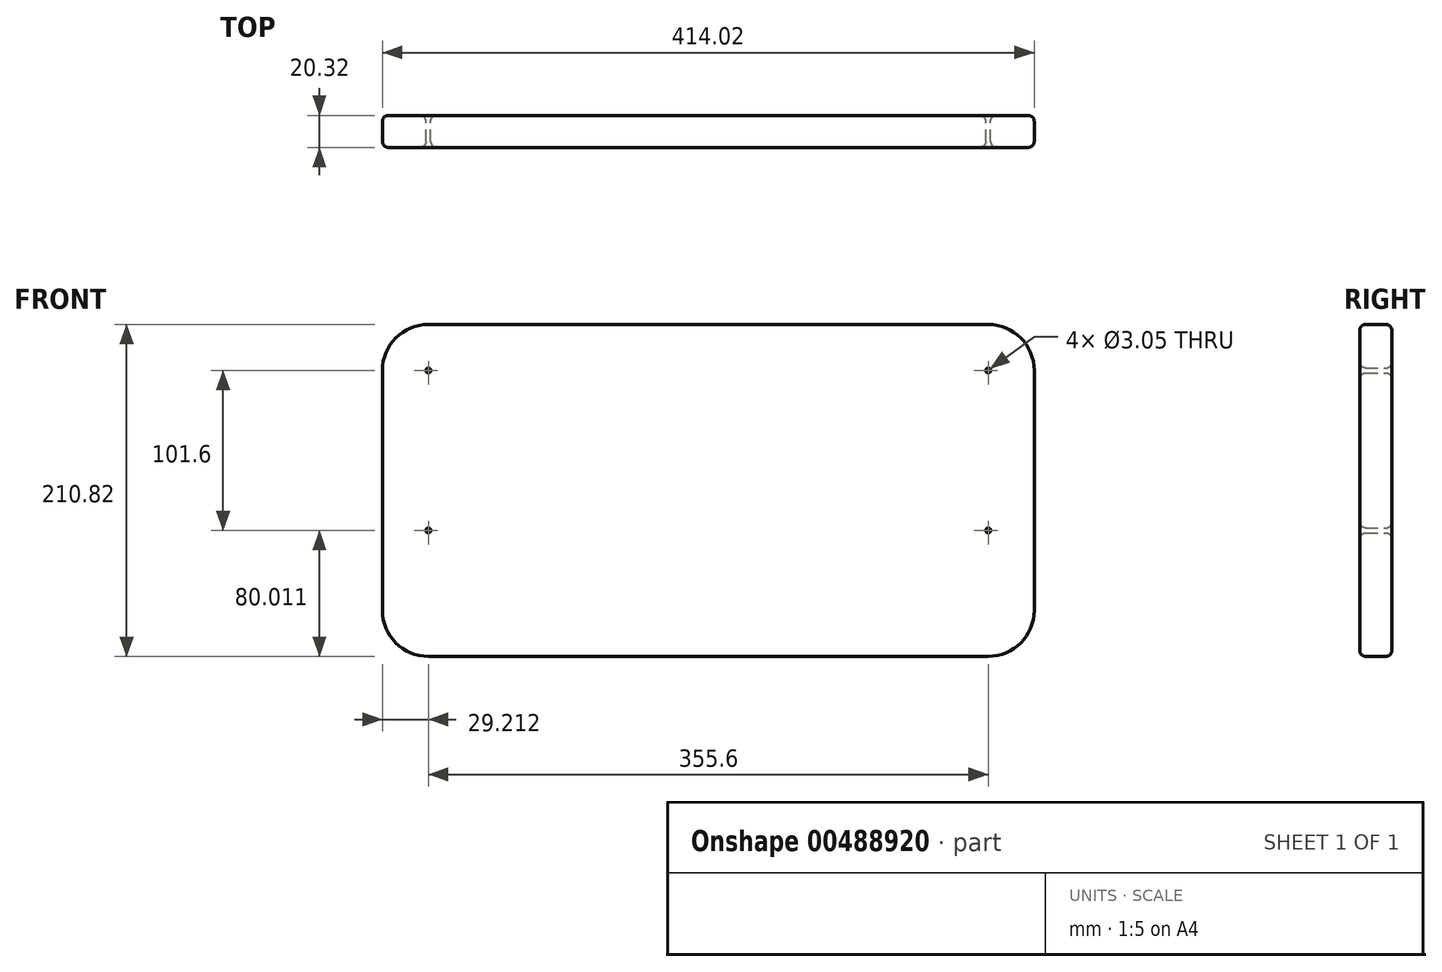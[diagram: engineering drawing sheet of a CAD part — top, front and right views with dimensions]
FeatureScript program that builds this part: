
annotation { "Feature Type Name" : "Feature", "Feature Type Description" : "" }
export const myFeature = defineFeature(function(context is Context, id is Id, definition is map)
    precondition{}
    {
        {
            var Q0;
            Q0=qCreatedBy(makeId("Front.planeOp"),FACE);
            var sketch = newSketch(context, id + "F0", { "sketchPlane" : qUnion([Q0])});
            skArc(sketch, "E0", {"start": v(-339, -245.28) * mm, "mid": v(-359.66, -253.83) * mm, "end": v(-368.22, -274.49) * mm});
            skArc(sketch, "E1", {"start": v(16.6, -245.28) * mm, "mid": v(37.25, -253.83) * mm, "end": v(45.8, -274.49) * mm});
            skLineSegment(sketch, "E2", {"start": v(-339, -245.28) * mm, "end": v(16.6, -245.28) * mm});
            skArc(sketch, "E3", {"start": v(-368.22, -426.89) * mm, "mid": v(-359.66, -447.54) * mm, "end": v(-339, -456.1) * mm});
            skArc(sketch, "E4", {"start": v(16.6, -456.1) * mm, "mid": v(37.25, -447.54) * mm, "end": v(45.8, -426.89) * mm});
            skLineSegment(sketch, "E5", {"start": v(-368.22, -274.49) * mm, "end": v(-368.22, -426.89) * mm});
            skLineSegment(sketch, "E6", {"start": v(-339, -456.1) * mm, "end": v(16.6, -456.1) * mm});
            skLineSegment(sketch, "E7", {"start": v(45.8, -274.49) * mm, "end": v(45.8, -426.89) * mm});
            skCircle(sketch, "E8", {"center": v(-339, -274.49) * mm, "radius": 1.52 * mm});
            skCircle(sketch, "E9", {"center": v(16.6, -274.49) * mm, "radius": 1.52 * mm});
            skCircle(sketch, "E10", {"center": v(-339, -376.09) * mm, "radius": 1.52 * mm});
            skPoint(sketch, "E11", {"position": v(-161.2, -245.28) * mm});
            skCircle(sketch, "E12.MirrorC", {"center": v(16.6, -376.09) * mm, "radius": 1.52 * mm});
            skSolve(sketch);
        }
        {
            var Q0;
            {var subQ1=sQuery(id+"F0.wireOp",EDGE,"sNFvKARg-ezan-HJEH-VfS0-Z6MDpd9502FD.top");Q0=makeQuery(id+"F0.imprint","IMPRINT",FACE,{"disambiguationData":[TD([[makeQuery(id+"F0.imprint","IMPRINT",EDGE,{"derivedFrom":subQ1}),1.0]])]});}
            var Q1;
            Q1=makeQuery(id+"F0.imprint","IMPRINT",FACE,{"disambiguationData":[TD([[makeQuery(id+"F0.imprint","IMPRINT",EDGE,{"derivedFrom":sQuery(id+"F0.wireOp",EDGE,"E0")}),1.0]])]});
            var Q2;
            {var subQ1=sQuery(id+"F0.wireOp",EDGE,"sNFvKARg-ezan-HJEH-VfS0-Z6MDpd9502FD.top");Q2=makeQuery(id+"F0.imprint","IMPRINT",FACE,{"disambiguationData":[TD([[makeQuery(id+"F0.imprint","IMPRINT",EDGE,{"derivedFrom":subQ1}),-1.0]])]});}
            extrude(context, id + "F1", {"entities" : qUnion([Q0, Q1, Q2]), "endBound" : BoundingType.SYMMETRIC, "depth" : 20.32 * mm});
        }
        {
            var Q0;
            Q0=makeQuery(id+"F1.opExtrude","CAP_FACE",FACE,{"disambiguationData":[OSD([sQuery(id+"F0.wireOp",EDGE,"E0"),sQuery(id+"F0.wireOp",EDGE,"E1"),sQuery(id+"F0.wireOp",EDGE,"E2"),sQuery(id+"F0.wireOp",EDGE,"E3"),sQuery(id+"F0.wireOp",EDGE,"E4"),sQuery(id+"F0.wireOp",EDGE,"E5"),sQuery(id+"F0.wireOp",EDGE,"E6"),sQuery(id+"F0.wireOp",EDGE,"E7"),sQuery(id+"F0.wireOp",EDGE,"E8"),sQuery(id+"F0.wireOp",EDGE,"uPIstdWG-PvQV-QiUX-S8yo-uPuZu8CxHxGs"),sQuery(id+"F0.wireOp",EDGE,"nMFlWxz2-jA4v-4VUK-rhDa-qOuRUuO9Ryie"),sQuery(id+"F0.wireOp",EDGE,"E9")])],"isStart":false});
            fillet(context, id + "F2", {"entities" : qUnion([Q0]), "radius" : 3.8 * mm, "tangentPropagation" : true, "allowEdgeOverflow" : false});
        }
        {
            var Q0;
            Q0=makeQuery(id+"F1.opExtrude","CAP_FACE",FACE,{"disambiguationData":[OSD([sQuery(id+"F0.wireOp",EDGE,"E0"),sQuery(id+"F0.wireOp",EDGE,"E1"),sQuery(id+"F0.wireOp",EDGE,"E2"),sQuery(id+"F0.wireOp",EDGE,"E3"),sQuery(id+"F0.wireOp",EDGE,"E4"),sQuery(id+"F0.wireOp",EDGE,"E5"),sQuery(id+"F0.wireOp",EDGE,"E6"),sQuery(id+"F0.wireOp",EDGE,"E7"),sQuery(id+"F0.wireOp",EDGE,"E8"),sQuery(id+"F0.wireOp",EDGE,"uPIstdWG-PvQV-QiUX-S8yo-uPuZu8CxHxGs"),sQuery(id+"F0.wireOp",EDGE,"nMFlWxz2-jA4v-4VUK-rhDa-qOuRUuO9Ryie"),sQuery(id+"F0.wireOp",EDGE,"E9")])],"isStart":true});
            var Q1;
            Q1=makeQuery(id+"F2.opFillet","BLEND_FACE",FACE,{"disambiguationData":[OSD([sQuery(id+"F0.wireOp",EDGE,"E3")])]});
            fillet(context, id + "F3", {"entities" : qUnion([Q0, Q1]), "radius" : 3.8 * mm, "tangentPropagation" : true, "allowEdgeOverflow" : false});
        }
    });
